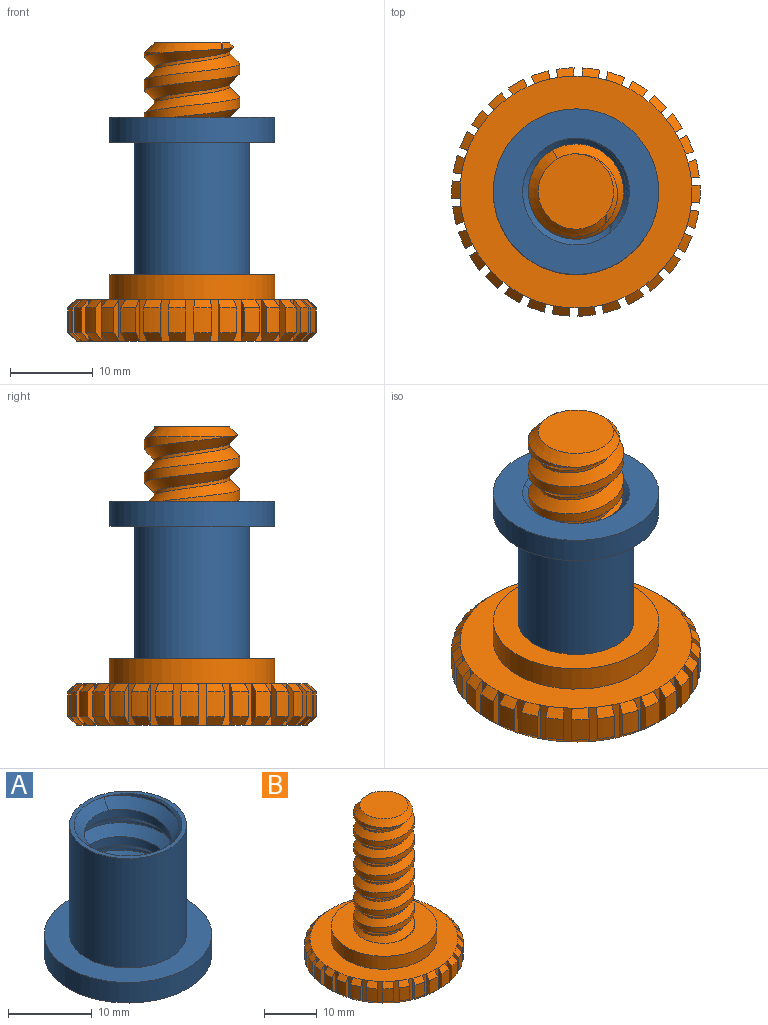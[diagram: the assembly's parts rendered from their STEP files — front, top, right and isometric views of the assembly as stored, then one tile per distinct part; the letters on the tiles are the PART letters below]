
ASSEMBLY  parts=2 mates=1
PART A: 11 faces, bbox 20x20x22.1 mm
  f0: cylinder r=10mm len=20mm, axis (0,0,-1), area 188.5mm2, adj f1,f2
  f1: plane 20x20mm, normal (0,0,1), area 160.2mm2, adj f0,f4
  f2: plane 20x20mm, normal (0,0,-1), area 183.5mm2, adj f0,f6,f10
  f3: cylinder r=5.25mm len=16.6mm, axis (0,0,-1), area 160.7mm2, adj f6,f7,f8,f9
  f4: cylinder r=7mm len=16mm, axis (0,0,-1), area 703.7mm2, adj f1,f5
  f5: plane 14x14mm, normal (0,0,1), area 23.2mm2, adj f4,f7,f10
  f6: cone r=6.45mm half-angle=45deg, axis (0,0,-1), area 38mm2, adj f2,f3,f8,f9
  f7: cone r=5.25mm half-angle=45deg, axis (0,0,1), area 38.2mm2, adj f3,f5,f8,f9
  f8: bspline ~21.2x14.9mm, area 279.1mm2, adj f3,f6,f7,f10
  f9: bspline ~20.53x14.9mm, area 279.2mm2, adj f3,f6,f7,f10
  f10: cylinder r=6.45mm len=19mm, axis (0,0,-1), area 75.6mm2, adj f2,f5,f8,f9
PART B: 192 faces, bbox 30x30x37.3 mm
  f0: plane 28x27.98mm, normal (0,0,1), area 301.4mm2, adj f3,f6,f9,f12,f15,f18,f21,f24
  f1: plane 28x27.98mm, normal (0,0,-1), area 615.6mm2, adj f2,f5,f8,f11,f14,f17,f20,f23
  f2: cone r=15mm half-angle=45deg, axis (0,0,1), area 2.9mm2, adj f1,f89,f102,f191
  f3: cone r=14mm half-angle=45deg, axis (0,0,-1), area 2.9mm2, adj f0,f89,f102,f191
  f4: cylinder r=15mm len=3mm, axis (0,0,-1), area 6.4mm2, adj f5,f6,f188,f189
  f5: cone r=15mm half-angle=45deg, axis (0,0,1), area 2.9mm2, adj f1,f4,f188,f189
  f6: cone r=14mm half-angle=45deg, axis (0,0,-1), area 2.9mm2, adj f0,f4,f188,f189
  f7: cylinder r=15mm len=3mm, axis (0,0,-1), area 6.4mm2, adj f8,f9,f185,f186
  f8: cone r=15mm half-angle=45deg, axis (0,0,1), area 2.9mm2, adj f1,f7,f185,f186
  f9: cone r=14mm half-angle=45deg, axis (0,0,-1), area 2.9mm2, adj f0,f7,f185,f186
  f10: cylinder r=15mm len=3mm, axis (0,0,-1), area 6.4mm2, adj f11,f12,f182,f183
  f11: cone r=15mm half-angle=45deg, axis (0,0,1), area 2.9mm2, adj f1,f10,f182,f183
  f12: cone r=14mm half-angle=45deg, axis (0,0,-1), area 2.9mm2, adj f0,f10,f182,f183
  f13: cylinder r=15mm len=3mm, axis (0,0,-1), area 6.4mm2, adj f14,f15,f179,f180
  f14: cone r=15mm half-angle=45deg, axis (0,0,1), area 2.9mm2, adj f1,f13,f179,f180
  f15: cone r=14mm half-angle=45deg, axis (0,0,-1), area 2.9mm2, adj f0,f13,f179,f180
  f16: cylinder r=15mm len=3mm, axis (0,0,-1), area 6.4mm2, adj f17,f18,f176,f177
  f17: cone r=15mm half-angle=45deg, axis (0,0,1), area 2.9mm2, adj f1,f16,f176,f177
  f18: cone r=14mm half-angle=45deg, axis (0,0,-1), area 2.9mm2, adj f0,f16,f176,f177
  f19: cylinder r=15mm len=3mm, axis (0,0,-1), area 6.4mm2, adj f20,f21,f173,f174
  f20: cone r=15mm half-angle=45deg, axis (0,0,1), area 2.9mm2, adj f1,f19,f173,f174
  f21: cone r=14mm half-angle=45deg, axis (0,0,-1), area 2.9mm2, adj f0,f19,f173,f174
  f22: cylinder r=15mm len=3mm, axis (0,0,-1), area 6.4mm2, adj f23,f24,f170,f171
  f23: cone r=15mm half-angle=45deg, axis (0,0,1), area 2.9mm2, adj f1,f22,f170,f171
  f24: cone r=14mm half-angle=45deg, axis (0,0,-1), area 2.9mm2, adj f0,f22,f170,f171
  f25: cylinder r=15mm len=3mm, axis (0,0,-1), area 6.4mm2, adj f26,f27,f167,f168
  f26: cone r=15mm half-angle=45deg, axis (0,0,1), area 2.9mm2, adj f1,f25,f167,f168
  f27: cone r=14mm half-angle=45deg, axis (0,0,-1), area 2.9mm2, adj f0,f25,f167,f168
  f28: cylinder r=15mm len=3mm, axis (0,0,-1), area 6.4mm2, adj f29,f30,f164,f165
  f29: cone r=15mm half-angle=45deg, axis (0,0,1), area 2.9mm2, adj f1,f28,f164,f165
  f30: cone r=14mm half-angle=45deg, axis (0,0,-1), area 2.9mm2, adj f0,f28,f164,f165
  f31: cylinder r=15mm len=3mm, axis (0,0,-1), area 6.4mm2, adj f32,f33,f161,f162
  f32: cone r=15mm half-angle=45deg, axis (0,0,1), area 2.9mm2, adj f1,f31,f161,f162
  f33: cone r=14mm half-angle=45deg, axis (0,0,-1), area 2.9mm2, adj f0,f31,f161,f162
  f34: cylinder r=15mm len=3mm, axis (0,0,-1), area 6.4mm2, adj f35,f36,f158,f159
  f35: cone r=15mm half-angle=45deg, axis (0,0,1), area 2.9mm2, adj f1,f34,f158,f159
  f36: cone r=14mm half-angle=45deg, axis (0,0,-1), area 2.9mm2, adj f0,f34,f158,f159
  f37: cylinder r=15mm len=3mm, axis (0,0,-1), area 6.4mm2, adj f38,f39,f155,f156
  f38: cone r=15mm half-angle=45deg, axis (0,0,1), area 2.9mm2, adj f1,f37,f155,f156
  f39: cone r=14mm half-angle=45deg, axis (0,0,-1), area 2.9mm2, adj f0,f37,f155,f156
  f40: cylinder r=15mm len=3mm, axis (0,0,-1), area 6.4mm2, adj f41,f42,f152,f153
  f41: cone r=15mm half-angle=45deg, axis (0,0,1), area 2.9mm2, adj f1,f40,f152,f153
  f42: cone r=14mm half-angle=45deg, axis (0,0,-1), area 2.9mm2, adj f0,f40,f152,f153
  f43: cylinder r=15mm len=3mm, axis (0,0,-1), area 6.4mm2, adj f44,f45,f149,f150
  f44: cone r=15mm half-angle=45deg, axis (0,0,1), area 2.9mm2, adj f1,f43,f149,f150
  f45: cone r=14mm half-angle=45deg, axis (0,0,-1), area 2.9mm2, adj f0,f43,f149,f150
  f46: cylinder r=15mm len=3mm, axis (0,0,-1), area 6.4mm2, adj f47,f48,f146,f147
  f47: cone r=15mm half-angle=45deg, axis (0,0,1), area 2.9mm2, adj f1,f46,f146,f147
  f48: cone r=14mm half-angle=45deg, axis (0,0,-1), area 2.9mm2, adj f0,f46,f146,f147
  f49: cylinder r=15mm len=3mm, axis (0,0,-1), area 6.4mm2, adj f50,f51,f143,f144
  f50: cone r=15mm half-angle=45deg, axis (0,0,1), area 2.9mm2, adj f1,f49,f143,f144
  f51: cone r=14mm half-angle=45deg, axis (0,0,-1), area 2.9mm2, adj f0,f49,f143,f144
  f52: cylinder r=15mm len=3mm, axis (0,0,-1), area 6.4mm2, adj f53,f54,f140,f141
  f53: cone r=15mm half-angle=45deg, axis (0,0,1), area 2.9mm2, adj f1,f52,f140,f141
  f54: cone r=14mm half-angle=45deg, axis (0,0,-1), area 2.9mm2, adj f0,f52,f140,f141
  f55: cylinder r=15mm len=3mm, axis (0,0,-1), area 6.4mm2, adj f56,f57,f137,f138
  f56: cone r=15mm half-angle=45deg, axis (0,0,1), area 2.9mm2, adj f1,f55,f137,f138
  f57: cone r=14mm half-angle=45deg, axis (0,0,-1), area 2.9mm2, adj f0,f55,f137,f138
  f58: cylinder r=15mm len=3mm, axis (0,0,-1), area 6.4mm2, adj f59,f60,f134,f135
  f59: cone r=15mm half-angle=45deg, axis (0,0,1), area 2.9mm2, adj f1,f58,f134,f135
  f60: cone r=14mm half-angle=45deg, axis (0,0,-1), area 2.9mm2, adj f0,f58,f134,f135
  f61: cylinder r=15mm len=3mm, axis (0,0,-1), area 6.4mm2, adj f62,f63,f131,f132
  f62: cone r=15mm half-angle=45deg, axis (0,0,1), area 2.9mm2, adj f1,f61,f131,f132
  f63: cone r=14mm half-angle=45deg, axis (0,0,-1), area 2.9mm2, adj f0,f61,f131,f132
  f64: cylinder r=15mm len=3mm, axis (0,0,-1), area 6.4mm2, adj f65,f66,f128,f129
  f65: cone r=15mm half-angle=45deg, axis (0,0,1), area 2.9mm2, adj f1,f64,f128,f129
  f66: cone r=14mm half-angle=45deg, axis (0,0,-1), area 2.9mm2, adj f0,f64,f128,f129
  f67: cylinder r=15mm len=3mm, axis (0,0,-1), area 6.4mm2, adj f68,f69,f125,f126
  f68: cone r=15mm half-angle=45deg, axis (0,0,1), area 2.9mm2, adj f1,f67,f125,f126
  f69: cone r=14mm half-angle=45deg, axis (0,0,-1), area 2.9mm2, adj f0,f67,f125,f126
  f70: cylinder r=15mm len=3mm, axis (0,0,-1), area 6.4mm2, adj f71,f72,f122,f123
  f71: cone r=15mm half-angle=45deg, axis (0,0,1), area 2.9mm2, adj f1,f70,f122,f123
  f72: cone r=14mm half-angle=45deg, axis (0,0,-1), area 2.9mm2, adj f0,f70,f122,f123
  f73: cylinder r=15mm len=3mm, axis (0,0,-1), area 6.4mm2, adj f74,f75,f119,f120
  f74: cone r=15mm half-angle=45deg, axis (0,0,1), area 2.9mm2, adj f1,f73,f119,f120
  f75: cone r=14mm half-angle=45deg, axis (0,0,-1), area 2.9mm2, adj f0,f73,f119,f120
  f76: cylinder r=15mm len=3mm, axis (0,0,-1), area 6.4mm2, adj f77,f78,f116,f117
  f77: cone r=15mm half-angle=45deg, axis (0,0,1), area 2.9mm2, adj f1,f76,f116,f117
  f78: cone r=14mm half-angle=45deg, axis (0,0,-1), area 2.9mm2, adj f0,f76,f116,f117
  f79: cylinder r=15mm len=3mm, axis (0,0,-1), area 6.4mm2, adj f80,f81,f113,f114
  f80: cone r=15mm half-angle=45deg, axis (0,0,1), area 2.9mm2, adj f1,f79,f113,f114
  f81: cone r=14mm half-angle=45deg, axis (0,0,-1), area 2.9mm2, adj f0,f79,f113,f114
  f82: cylinder r=15mm len=3mm, axis (0,0,-1), area 6.4mm2, adj f83,f84,f110,f111
  f83: cone r=15mm half-angle=45deg, axis (0,0,1), area 2.9mm2, adj f1,f82,f110,f111
  f84: cone r=14mm half-angle=45deg, axis (0,0,-1), area 2.9mm2, adj f0,f82,f110,f111
  f85: cylinder r=15mm len=3mm, axis (0,0,-1), area 6.4mm2, adj f87,f88,f107,f108
  f86: cylinder r=15mm len=3mm, axis (0,0,-1), area 6.4mm2, adj f100,f101,f104,f105
  f87: cone r=15mm half-angle=45deg, axis (0,0,1), area 2.9mm2, adj f1,f85,f107,f108
  f88: cone r=14mm half-angle=45deg, axis (0,0,-1), area 2.9mm2, adj f0,f85,f107,f108
  f89: cylinder r=15mm len=3mm, axis (0,0,-1), area 6.4mm2, adj f2,f3,f102,f191
  f90: cylinder r=5.75mm len=26.8mm, axis (0,0,-1), area 417.9mm2, adj f92,f94,f96,f98
  f91: cylinder r=10mm len=20mm, axis (0,0,-1), area 188.5mm2, adj f0,f92
  f92: plane 20x20mm, normal (0,0,1), area 210.3mm2, adj f90,f91,f97
  f93: plane 9.1x9.1mm, normal (0,0,1), area 65mm2, adj f94,f99
  f94: cone r=4.55mm half-angle=45deg, axis (0,0,-1), area 32.3mm2, adj f90,f93,f96,f98
  f95: plane 2.8x1.2mm, normal (0,1,0), area 1.9mm2, adj f96,f97,f98,f99
  f96: bspline ~30.53x13.28mm, area 381.9mm2, adj f90,f94,f95,f99
  f97: cylinder r=5.75mm len=11.5mm, axis (0,0,1), area 35.5mm2, adj f92,f95,f98
  f98: bspline ~31.2x13.28mm, area 407.7mm2, adj f90,f94,f95,f97,f99
  f99: cylinder r=4.55mm len=29.6mm, axis (0,0,1), area -4.3mm2, adj f93,f95,f96,f98
  f100: cone r=15mm half-angle=45deg, axis (0,0,1), area 2.9mm2, adj f1,f86,f104,f105
  f101: cone r=14mm half-angle=45deg, axis (0,0,-1), area 2.9mm2, adj f0,f86,f104,f105
  f102: plane 5.02x1.03mm, normal (1,0,0), area 4mm2, adj f2,f3,f89,f103
  f103: plane 5x1mm, normal (0,-1,0), area 5mm2, adj f0,f1,f102,f104
  f104: plane 5.02x1.03mm, normal (-1,0,0), area 4mm2, adj f86,f100,f101,f103
  f105: plane 5.02x1mm, normal (0.98,0.21,0), area 4mm2, adj f86,f100,f101,f106
  f106: plane 5x0.98mm, normal (0.21,-0.98,0), area 5mm2, adj f0,f1,f105,f107
  f107: plane 5.02x1mm, normal (-0.98,-0.21,0), area 4mm2, adj f85,f87,f88,f106
  f108: plane 5.02x0.94mm, normal (0.91,0.41,0), area 4mm2, adj f85,f87,f88,f109
  f109: plane 5x0.91mm, normal (0.41,-0.91,0), area 5mm2, adj f0,f1,f108,f110
  f110: plane 5.02x0.94mm, normal (-0.91,-0.41,0), area 4mm2, adj f82,f83,f84,f109
  f111: plane 5.02x0.83mm, normal (0.81,0.59,0), area 4mm2, adj f82,f83,f84,f112
  f112: plane 5x0.81mm, normal (0.59,-0.81,0), area 5mm2, adj f0,f1,f111,f113
  f113: plane 5.02x0.83mm, normal (-0.81,-0.59,0), area 4mm2, adj f79,f80,f81,f112
  f114: plane 5.02x0.77mm, normal (0.67,0.74,0), area 4mm2, adj f79,f80,f81,f115
  f115: plane 5x0.74mm, normal (0.74,-0.67,0), area 5mm2, adj f0,f1,f114,f116
  f116: plane 5.02x0.77mm, normal (-0.67,-0.74,0), area 4mm2, adj f76,f77,f78,f115
  f117: plane 5.02x0.89mm, normal (0.5,0.87,0), area 4mm2, adj f76,f77,f78,f118
  f118: plane 5x0.87mm, normal (0.87,-0.5,0), area 5mm2, adj f0,f1,f117,f119
  f119: plane 5.02x0.89mm, normal (-0.5,-0.87,0), area 4mm2, adj f73,f74,f75,f118
  f120: plane 5.02x0.98mm, normal (0.31,0.95,0), area 4mm2, adj f73,f74,f75,f121
  f121: plane 5x0.95mm, normal (0.95,-0.31,0), area 5mm2, adj f0,f1,f120,f122
  f122: plane 5.02x0.98mm, normal (-0.31,-0.95,0), area 4mm2, adj f70,f71,f72,f121
  f123: plane 5.02x1.02mm, normal (0.1,0.99,0), area 4mm2, adj f70,f71,f72,f124
  f124: plane 5x0.99mm, normal (0.99,-0.1,0), area 5mm2, adj f0,f1,f123,f125
  f125: plane 5.02x1.02mm, normal (-0.1,-0.99,0), area 4mm2, adj f67,f68,f69,f124
  f126: plane 5.02x1.02mm, normal (-0.1,0.99,0), area 4mm2, adj f67,f68,f69,f127
  f127: plane 5x0.99mm, normal (0.99,0.1,0), area 5mm2, adj f0,f1,f126,f128
  f128: plane 5.02x1.02mm, normal (0.1,-0.99,0), area 4mm2, adj f64,f65,f66,f127
  f129: plane 5.02x0.98mm, normal (-0.31,0.95,0), area 4mm2, adj f64,f65,f66,f130
  f130: plane 5x0.95mm, normal (0.95,0.31,0), area 5mm2, adj f0,f1,f129,f131
  f131: plane 5.02x0.98mm, normal (0.31,-0.95,0), area 4mm2, adj f61,f62,f63,f130
  f132: plane 5.02x0.89mm, normal (-0.5,0.87,0), area 4mm2, adj f61,f62,f63,f133
  f133: plane 5x0.87mm, normal (0.87,0.5,0), area 5mm2, adj f0,f1,f132,f134
  f134: plane 5.02x0.89mm, normal (0.5,-0.87,0), area 4mm2, adj f58,f59,f60,f133
  f135: plane 5.02x0.77mm, normal (-0.67,0.74,0), area 4mm2, adj f58,f59,f60,f136
  f136: plane 5x0.74mm, normal (0.74,0.67,0), area 5mm2, adj f0,f1,f135,f137
  f137: plane 5.02x0.77mm, normal (0.67,-0.74,0), area 4mm2, adj f55,f56,f57,f136
  f138: plane 5.02x0.83mm, normal (-0.81,0.59,0), area 4mm2, adj f55,f56,f57,f139
  f139: plane 5x0.81mm, normal (0.59,0.81,0), area 5mm2, adj f0,f1,f138,f140
  f140: plane 5.02x0.83mm, normal (0.81,-0.59,0), area 4mm2, adj f52,f53,f54,f139
  f141: plane 5.02x0.94mm, normal (-0.91,0.41,0), area 4mm2, adj f52,f53,f54,f142
  f142: plane 5x0.91mm, normal (0.41,0.91,0), area 5mm2, adj f0,f1,f141,f143
  f143: plane 5.02x0.94mm, normal (0.91,-0.41,0), area 4mm2, adj f49,f50,f51,f142
  f144: plane 5.02x1mm, normal (-0.98,0.21,0), area 4mm2, adj f49,f50,f51,f145
  f145: plane 5x0.98mm, normal (0.21,0.98,0), area 5mm2, adj f0,f1,f144,f146
  f146: plane 5.02x1mm, normal (0.98,-0.21,0), area 4mm2, adj f46,f47,f48,f145
  f147: plane 5.02x1.03mm, normal (-1,0,0), area 4mm2, adj f46,f47,f48,f148
  f148: plane 5x1mm, normal (0,1,0), area 5mm2, adj f0,f1,f147,f149
  f149: plane 5.02x1.03mm, normal (1,0,0), area 4mm2, adj f43,f44,f45,f148
  f150: plane 5.02x1mm, normal (-0.98,-0.21,0), area 4mm2, adj f43,f44,f45,f151
  f151: plane 5x0.98mm, normal (-0.21,0.98,0), area 5mm2, adj f0,f1,f150,f152
  f152: plane 5.02x1mm, normal (0.98,0.21,0), area 4mm2, adj f40,f41,f42,f151
  f153: plane 5.02x0.94mm, normal (-0.91,-0.41,0), area 4mm2, adj f40,f41,f42,f154
  f154: plane 5x0.91mm, normal (-0.41,0.91,0), area 5mm2, adj f0,f1,f153,f155
  f155: plane 5.02x0.94mm, normal (0.91,0.41,0), area 4mm2, adj f37,f38,f39,f154
  f156: plane 5.02x0.83mm, normal (-0.81,-0.59,0), area 4mm2, adj f37,f38,f39,f157
  f157: plane 5x0.81mm, normal (-0.59,0.81,0), area 5mm2, adj f0,f1,f156,f158
  f158: plane 5.02x0.83mm, normal (0.81,0.59,0), area 4mm2, adj f34,f35,f36,f157
  f159: plane 5.02x0.77mm, normal (-0.67,-0.74,0), area 4mm2, adj f34,f35,f36,f160
  f160: plane 5x0.74mm, normal (-0.74,0.67,0), area 5mm2, adj f0,f1,f159,f161
  f161: plane 5.02x0.77mm, normal (0.67,0.74,0), area 4mm2, adj f31,f32,f33,f160
  f162: plane 5.02x0.89mm, normal (-0.5,-0.87,0), area 4mm2, adj f31,f32,f33,f163
  f163: plane 5x0.87mm, normal (-0.87,0.5,0), area 5mm2, adj f0,f1,f162,f164
  f164: plane 5.02x0.89mm, normal (0.5,0.87,0), area 4mm2, adj f28,f29,f30,f163
  f165: plane 5.02x0.98mm, normal (-0.31,-0.95,0), area 4mm2, adj f28,f29,f30,f166
  f166: plane 5x0.95mm, normal (-0.95,0.31,0), area 5mm2, adj f0,f1,f165,f167
  f167: plane 5.02x0.98mm, normal (0.31,0.95,0), area 4mm2, adj f25,f26,f27,f166
  f168: plane 5.02x1.02mm, normal (-0.1,-0.99,0), area 4mm2, adj f25,f26,f27,f169
  f169: plane 5x0.99mm, normal (-0.99,0.1,0), area 5mm2, adj f0,f1,f168,f170
  f170: plane 5.02x1.02mm, normal (0.1,0.99,0), area 4mm2, adj f22,f23,f24,f169
  f171: plane 5.02x1.02mm, normal (0.1,-0.99,0), area 4mm2, adj f22,f23,f24,f172
  f172: plane 5x0.99mm, normal (-0.99,-0.1,0), area 5mm2, adj f0,f1,f171,f173
  f173: plane 5.02x1.02mm, normal (-0.1,0.99,0), area 4mm2, adj f19,f20,f21,f172
  f174: plane 5.02x0.98mm, normal (0.31,-0.95,0), area 4mm2, adj f19,f20,f21,f175
  f175: plane 5x0.95mm, normal (-0.95,-0.31,0), area 5mm2, adj f0,f1,f174,f176
  f176: plane 5.02x0.98mm, normal (-0.31,0.95,0), area 4mm2, adj f16,f17,f18,f175
  f177: plane 5.02x0.89mm, normal (0.5,-0.87,0), area 4mm2, adj f16,f17,f18,f178
  f178: plane 5x0.87mm, normal (-0.87,-0.5,0), area 5mm2, adj f0,f1,f177,f179
  f179: plane 5.02x0.89mm, normal (-0.5,0.87,0), area 4mm2, adj f13,f14,f15,f178
  f180: plane 5.02x0.77mm, normal (0.67,-0.74,0), area 4mm2, adj f13,f14,f15,f181
  f181: plane 5x0.74mm, normal (-0.74,-0.67,0), area 5mm2, adj f0,f1,f180,f182
  f182: plane 5.02x0.77mm, normal (-0.67,0.74,0), area 4mm2, adj f10,f11,f12,f181
  f183: plane 5.02x0.83mm, normal (0.81,-0.59,0), area 4mm2, adj f10,f11,f12,f184
  f184: plane 5x0.81mm, normal (-0.59,-0.81,0), area 5mm2, adj f0,f1,f183,f185
  f185: plane 5.02x0.83mm, normal (-0.81,0.59,0), area 4mm2, adj f7,f8,f9,f184
  f186: plane 5.02x0.94mm, normal (0.91,-0.41,0), area 4mm2, adj f7,f8,f9,f187
  f187: plane 5x0.91mm, normal (-0.41,-0.91,0), area 5mm2, adj f0,f1,f186,f188
  f188: plane 5.02x0.94mm, normal (-0.91,0.41,0), area 4mm2, adj f4,f5,f6,f187
  f189: plane 5.02x1mm, normal (0.98,-0.21,0), area 4mm2, adj f4,f5,f6,f190
  f190: plane 5x0.98mm, normal (-0.21,-0.98,0), area 5mm2, adj f0,f1,f189,f191
  f191: plane 5.02x1mm, normal (-0.98,0.21,0), area 4mm2, adj f2,f3,f89,f190
PLACE A rot(axis=(0.54,-0.84,0),180deg) t=(-62.73,11.16,25.12)mm
PLACE B rot(axis=(0,0,-1),25deg) t=(-23.31,22.95,-1.88)mm
MATE revolute B.f91 <-> A.f0  axis (0,0,1) through (-23.31,22.95,6.12)mm
